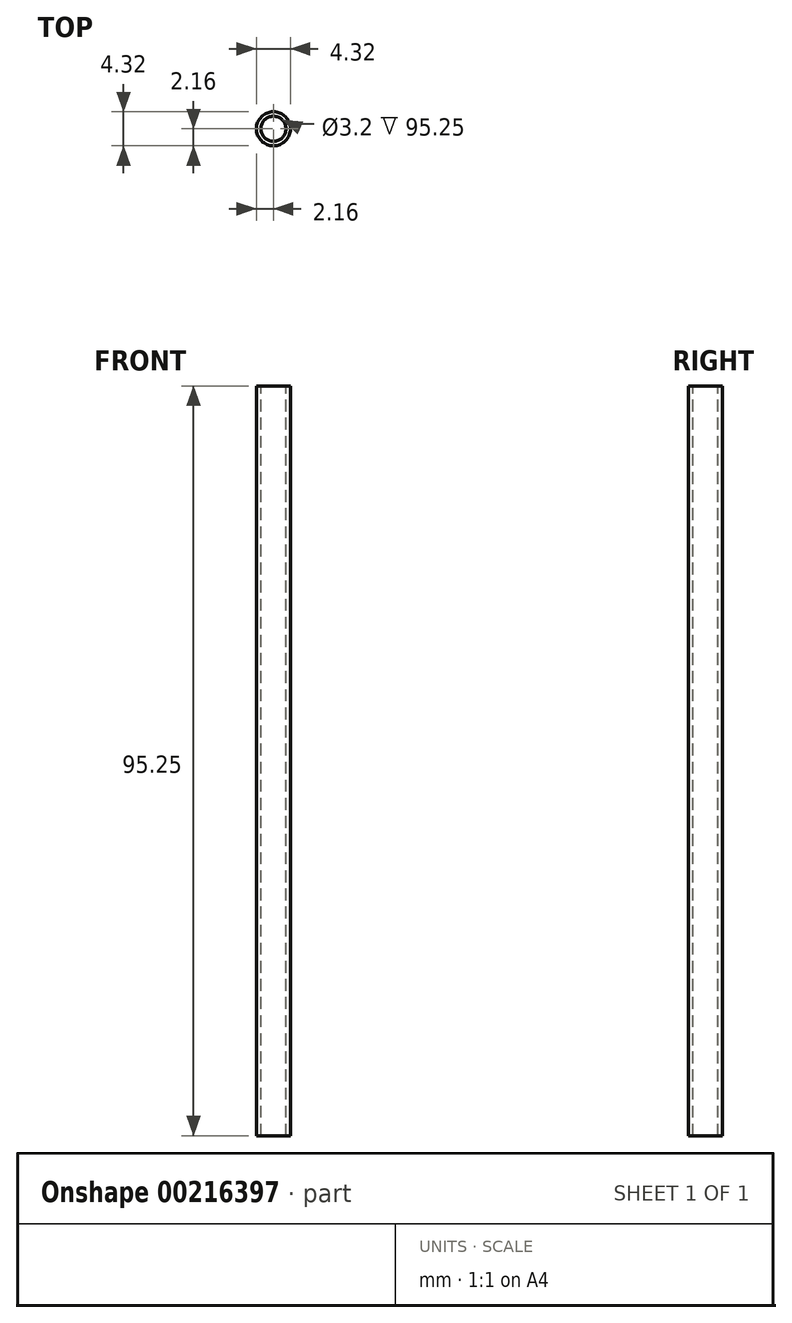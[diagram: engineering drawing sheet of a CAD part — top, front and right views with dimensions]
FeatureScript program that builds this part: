
annotation { "Feature Type Name" : "Feature", "Feature Type Description" : "" }
export const myFeature = defineFeature(function(context is Context, id is Id, definition is map)
    precondition{}
    {
        {
            var Q0;
            Q0=qCreatedBy(makeId("Top.planeOp"),FACE);
            var sketch = newSketch(context, id + "F0", { "sketchPlane" : qUnion([Q0])});
            skCircle(sketch, "E0", {"center": v(0, 0) * mm, "radius": 2.16 * mm});
            skSolve(sketch);
        }
        {
            var Q0;
            Q0 = qSketchRegion(id + "F0", true);
            extrude(context, id + "F1", {"entities" : qUnion([Q0]), "depth" : 95.25 * mm});
        }
        {
            var Q0;
            Q0=makeQuery(id+"F1.opExtrude","CAP_FACE",FACE,{"disambiguationData":[OSD([sQuery(id+"F0.wireOp",EDGE,"E0")])],"isStart":false});
            var sketch = newSketch(context, id + "F2", { "sketchPlane" : qUnion([Q0])});
            skPoint(sketch, "E1", {"position": v(0, 0) * mm});
            skSolve(sketch);
        }
        {
            var Q0;
            Q0=sQuery(id+"F2.wireOp",VERTEX,"E1");
            var Q1;
            Q1=makeQuery(id+"F1.opExtrude","SWEPT_BODY",BODY,{"disambiguationData":[OSD([sQuery(id+"F0.wireOp",EDGE,"E0")])]});
            hole(context, id + "F3", {"style" : HoleStyle.SIMPLE, "endStyle" : HoleEndStyle.BLIND, "standardTappedOrClearance" : lookupTablePath({ "standard" : "ISO", "engagement" : "75%", "pitch" : "0.75 mm", "size" : "M4", "type" : "Tapped" }), "standardBlindInLast" : lookupTablePath({ "standard" : "ISO", "engagement" : "75%", "pitch" : "0.75 mm", "size" : "M4", "type" : "Tapped" }), "holeDiameter" : 3.2 * mm, "showTappedDepth" : true, "holeDepth" : 103.85 * mm, "tappedDepth" : 101.6 * mm, "tapClearance" : 3, "locations" : qUnion([Q0]), "scope" : qUnion([Q1])});
        }
    });
